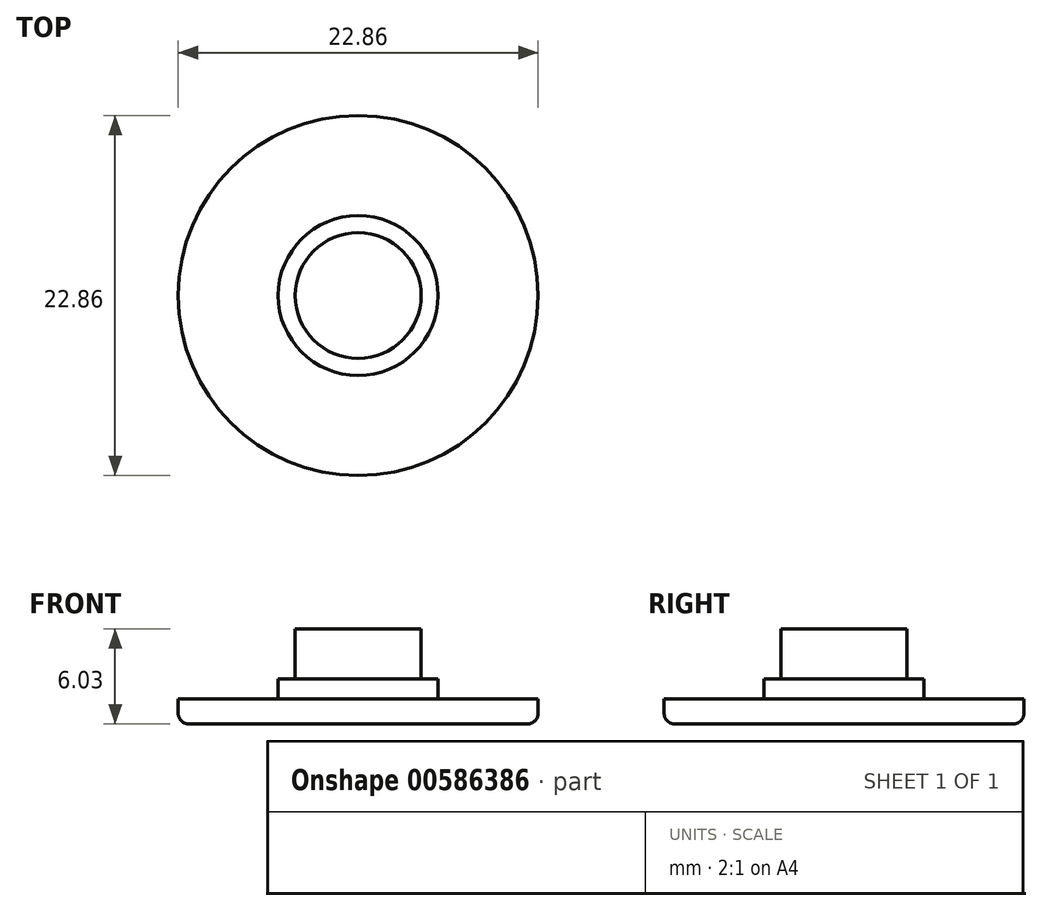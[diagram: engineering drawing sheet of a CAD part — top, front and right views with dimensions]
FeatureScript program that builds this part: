
annotation { "Feature Type Name" : "Feature", "Feature Type Description" : "" }
export const myFeature = defineFeature(function(context is Context, id is Id, definition is map)
    precondition{}
    {
        {
            var Q0;
            Q0=qCreatedBy(makeId("Top.planeOp"),FACE);
            var sketch = newSketch(context, id + "F0", { "sketchPlane" : qUnion([Q0])});
            skCircle(sketch, "E0", {"center": v(0, 0) * mm, "radius": 11.43 * mm});
            skSolve(sketch);
        }
        {
            var Q0;
            Q0=makeQuery(id+"F0.imprint","IMPRINT",FACE,{"disambiguationData":[TD([[makeQuery(id+"F0.imprint","IMPRINT",EDGE,{"derivedFrom":sQuery(id+"F0.wireOp",EDGE,"E0")}),1.0]])]});
            extrude(context, id + "F1", {"entities" : qUnion([Q0]), "depth" : 1.59 * mm, "offsetDistance" : 25.4 * mm});
        }
        {
            var Q0;
            Q0=makeQuery(id+"F1.opExtrude","CAP_FACE",FACE,{"disambiguationData":[OSD([sQuery(id+"F0.wireOp",EDGE,"E0")])],"isStart":false});
            var sketch = newSketch(context, id + "F2", { "sketchPlane" : qUnion([Q0])});
            skCircle(sketch, "E1", {"center": v(0, 0) * mm, "radius": 5.08 * mm});
            skSolve(sketch);
        }
        {
            var Q0;
            Q0=makeQuery(id+"F2.imprint","IMPRINT",FACE,{"disambiguationData":[TD([[makeQuery(id+"F2.imprint","IMPRINT",EDGE,{"derivedFrom":sQuery(id+"F2.wireOp",EDGE,"E1")}),1.0]])]});
            extrude(context, id + "F3", {"entities" : qUnion([Q0]), "operationType" : NewBodyOperationType.ADD, "depth" : 1.27 * mm, "offsetDistance" : 25.4 * mm});
        }
        {
            var Q0;
            Q0=makeQuery(id+"F3.opExtrude","CAP_FACE",FACE,{"disambiguationData":[OSD([sQuery(id+"F2.wireOp",EDGE,"E1")])],"isStart":false});
            var sketch = newSketch(context, id + "F4", { "sketchPlane" : qUnion([Q0])});
            skCircle(sketch, "E2", {"center": v(0, 0) * mm, "radius": 4 * mm});
            skSolve(sketch);
        }
        {
            var Q0;
            Q0 = qSketchRegion(id + "F4", true);
            extrude(context, id + "F5", {"entities" : qUnion([Q0]), "operationType" : NewBodyOperationType.ADD, "depth" : 3.17 * mm, "offsetDistance" : 25.4 * mm});
        }
        {
            var Q0;
            Q0=makeQuery(id+"F1.opExtrude","CAP_EDGE",EDGE,{"disambiguationData":[OSD([sQuery(id+"F0.wireOp",EDGE,"E0")])],"isStart":true});
            fillet(context, id + "F6", {"entities" : qUnion([Q0]), "radius" : 0.67 * mm, "tangentPropagation" : true, "allowEdgeOverflow" : false});
        }
    });
